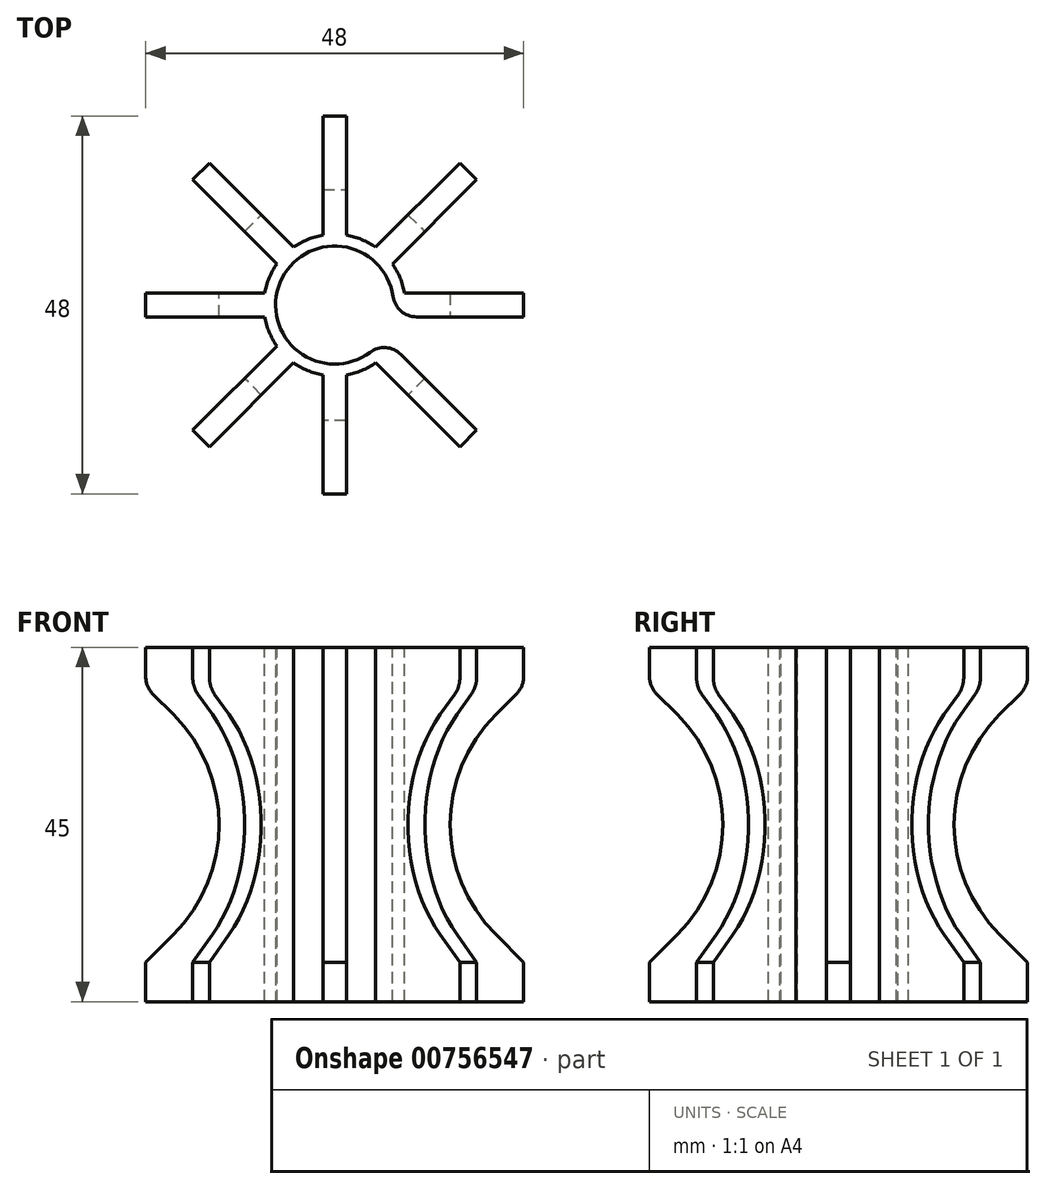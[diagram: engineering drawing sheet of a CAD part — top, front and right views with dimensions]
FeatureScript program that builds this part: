
annotation { "Feature Type Name" : "Feature", "Feature Type Description" : "" }
export const myFeature = defineFeature(function(context is Context, id is Id, definition is map)
    precondition{}
    {
        {
            assignVariable(context, id + "F0", {"name" : "h", "anyValue" : 45 * mm});
        }
        {
            assignVariable(context, id + "F1", {"name" : "t", "anyValue" : 1.5 * mm});
        }
        {
            assignVariable(context, id + "F2", {"name" : "fins", "anyValue" : 8});
        }
        {
            var Q0;
            Q0=qCreatedBy(makeId("Top.planeOp"),FACE);
            var sketch = newSketch(context, id + "F3", { "sketchPlane" : qUnion([Q0])});
            skCircle(sketch, "E0", {"center": v(0, 0) * mm, "radius": 7.5 * mm});
            skSolve(sketch);
        }
        {
            var Q0;
            Q0=makeQuery(id+"F3.imprint","IMPRINT",FACE,{"disambiguationData":[TD([[makeQuery(id+"F3.imprint","IMPRINT",EDGE,{"derivedFrom":sQuery(id+"F3.wireOp",EDGE,"E0")}),1.0]])]});
            extrude(context, id + "F4", {"entities" : qUnion([Q0]), "depth" : getVariable(context, 'h'), "offsetDistance" : 25 * mm});
        }
        {
            var Q0;
            Q0=makeQuery(id+"F4.opExtrude","CAP_FACE",FACE,{"disambiguationData":[OSD([sQuery(id+"F3.wireOp",EDGE,"E0")])],"isStart":false});
            var Q1;
            Q1=makeQuery(id+"F4.opExtrude","CAP_FACE",FACE,{"disambiguationData":[OSD([sQuery(id+"F3.wireOp",EDGE,"E0")])],"isStart":true});
            shell(context, id + "F5", {"entities" : qUnion([Q0, Q1]), "thickness" : getVariable(context, 't'), "oppositeDirection" : true});
        }
        {
            var Q0;
            Q0=makeQuery(id+"F4.opExtrude","CAP_FACE",FACE,{"disambiguationData":[OSD([sQuery(id+"F3.wireOp",EDGE,"E0")])],"isStart":false});
            var sketch = newSketch(context, id + "F6", { "sketchPlane" : qUnion([Q0])});
            skLineSegment(sketch, "E1.bottom", {"start": v(-1.5, 8.87) * mm, "end": v(1.5, 8.87) * mm});
            skLineSegment(sketch, "E1.top", {"start": v(-1.5, 24) * mm, "end": v(1.5, 24) * mm});
            skLineSegment(sketch, "E1.left", {"start": v(-1.5, 8.87) * mm, "end": v(-1.5, 24) * mm});
            skLineSegment(sketch, "E1.right", {"start": v(1.5, 8.87) * mm, "end": v(1.5, 24) * mm});
            skSolve(sketch);
        }
        {
            var Q0;
            Q0=qCreatedBy(makeId("Front.planeOp"),FACE);
            var sketch = newSketch(context, id + "F7", { "sketchPlane" : qUnion([Q0])});
            skLineSegment(sketch, "E2", {"start": v(0, 0) * mm, "end": v(0, 40.18) * mm});
            skSolve(sketch);
        }
        {
            var Q0;
            Q0 = qSketchRegion(id + "F6", true);
            var Q1;
            Q1=makeQuery(id+"F4.opExtrude","CAP_FACE",FACE,{"disambiguationData":[OSD([sQuery(id+"F3.wireOp",EDGE,"E0")])],"isStart":true});
            extrude(context, id + "F8", {"entities" : qUnion([Q0]), "operationType" : NewBodyOperationType.ADD, "endBound" : BoundingType.UP_TO_SURFACE, "oppositeDirection" : true, "depth" : 25 * mm, "endBoundEntityFace" : qUnion([Q1]), "offsetDistance" : 25 * mm});
        }
        {
            var Q0;
            Q0=makeQuery(id+"F8.opExtrude","SWEPT_FACE",FACE,{"disambiguationData":[OSD([sQuery(id+"F6.wireOp",EDGE,"E1.right")])]});
            var sketch = newSketch(context, id + "F9", { "sketchPlane" : qUnion([Q0])});
            skLineSegment(sketch, "E3", {"start": v(24, 5) * mm, "end": v(20.46, 8.54) * mm});
            skLineSegment(sketch, "E4", {"start": v(24, 40) * mm, "end": v(20.46, 36.46) * mm});
            skArc(sketch, "E5", {"start": v(20.46, 36.46) * mm, "mid": v(14.68, 22.5) * mm, "end": v(20.46, 8.54) * mm});
            skLineSegment(sketch, "E6", {"start": v(24, 5) * mm, "end": v(24, 40) * mm});
            skSolve(sketch);
        }
        {
            var Q0;
            Q0 = qSketchRegion(id + "F9", true);
            extrude(context, id + "F10", {"entities" : qUnion([Q0]), "operationType" : NewBodyOperationType.REMOVE, "endBound" : BoundingType.THROUGH_ALL, "oppositeDirection" : true, "depth" : 25 * mm, "offsetDistance" : 25 * mm});
        }
        {
            var Q0;
            Q0=makeQuery(id+"F10.boolean.opBoolean","COPY",EDGE,{"derivedFrom":makeQuery(id+"F10.opExtrude","SWEPT_EDGE",EDGE,{"disambiguationData":[OSD([sQuery(id+"F6.wireOp",EDGE,"E1.top"),sQuery(id+"F6.wireOp",EDGE,"E1.right"),sQuery(id+"F9.wireOp",EDGE,"E4"),sQuery(id+"F9.wireOp",EDGE,"E6")])]})});
            var Q1;
            Q1=makeQuery(id+"F10.boolean.opBoolean","COPY",EDGE,{"derivedFrom":makeQuery(id+"F10.opExtrude","SWEPT_EDGE",EDGE,{"disambiguationData":[OSD([sQuery(id+"F6.wireOp",EDGE,"E1.top"),sQuery(id+"F6.wireOp",EDGE,"E1.right"),sQuery(id+"F9.wireOp",EDGE,"E3"),sQuery(id+"F9.wireOp",EDGE,"E6")])]})});
            var Q2;
            Q2=makeQuery(id+"F8.opExtrude","SWEPT_EDGE",EDGE,{"disambiguationData":[OSD([sQuery(id+"F3.wireOp",EDGE,"E0"),sQuery(id+"F6.wireOp",EDGE,"E1.bottom"),sQuery(id+"F6.wireOp",EDGE,"E1.right")])]});
            var Q3;
            Q3=makeQuery(id+"F8.opExtrude","SWEPT_EDGE",EDGE,{"disambiguationData":[OSD([sQuery(id+"F3.wireOp",EDGE,"E0"),sQuery(id+"F6.wireOp",EDGE,"E1.bottom"),sQuery(id+"F6.wireOp",EDGE,"E1.left")])]});
            fillet(context, id + "F11", {"entities" : qUnion([Q0, Q1, Q2, Q3]), "radius" : getVariable(context, 't') * 2, "tangentPropagation" : true, "allowEdgeOverflow" : false});
        }
        {
            var Q0;
            Q0=makeQuery(id+"F4.opExtrude","SWEPT_BODY",BODY,{"disambiguationData":[OSD([sQuery(id+"F3.wireOp",EDGE,"E0")])]});
            var Q1;
            Q1=sQuery(id+"F7.wireOp",EDGE,"E2");
            circularPattern(context, id + "F12", {"operationType" : NewBodyOperationType.ADD, "entities" : qUnion([Q0]), "axis" : qUnion([Q1]), "angle" : 360 * degree, "instanceCount" : getVariable(context, 'fins'), "equalSpace" : true});
        }
        {
            var Q0;
            {var subQ0=makeQuery(id+"F8.opExtrude","CAP_FACE",FACE,{"disambiguationData":[OSD([sQuery(id+"F6.wireOp",EDGE,"E1.bottom"),sQuery(id+"F6.wireOp",EDGE,"E1.top"),sQuery(id+"F6.wireOp",EDGE,"E1.left"),sQuery(id+"F6.wireOp",EDGE,"E1.right")])],"isStart":true});Q0=makeQuery(id+"F12.boolean.opBoolean","MERGE",FACE,{"derivedFrom":[makeQuery(id+"F4.opExtrude","CAP_FACE",FACE,{"disambiguationData":[OSD([sQuery(id+"F3.wireOp",EDGE,"E0")])],"isStart":false}),subQ0,makeQuery(id+"F12.opPattern","COPY",FACE,{"derivedFrom":subQ0,"instanceName":"1"}),makeQuery(id+"F12.opPattern","COPY",FACE,{"derivedFrom":subQ0,"instanceName":"2"}),makeQuery(id+"F12.opPattern","COPY",FACE,{"derivedFrom":subQ0,"instanceName":"3"}),makeQuery(id+"F12.opPattern","COPY",FACE,{"derivedFrom":subQ0,"instanceName":"4"}),makeQuery(id+"F12.opPattern","COPY",FACE,{"derivedFrom":subQ0,"instanceName":"5"}),makeQuery(id+"F12.opPattern","COPY",FACE,{"derivedFrom":subQ0,"instanceName":"6"}),makeQuery(id+"F12.opPattern","COPY",FACE,{"derivedFrom":subQ0,"instanceName":"7"})]});}
            var sketch = newSketch(context, id + "F13", { "sketchPlane" : qUnion([Q0])});
            skLineSegment(sketch, "E7", {"start": v(18.03, -15.9) * mm, "end": v(3.62, -1.5) * mm});
            skLineSegment(sketch, "E8", {"start": v(24, -1.5) * mm, "end": v(3.62, -1.5) * mm});
            skLineSegment(sketch, "E9", {"start": v(18.03, -15.9) * mm, "end": v(24, -1.5) * mm});
            skSolve(sketch);
        }
        {
            var Q0;
            Q0 = qSketchRegion(id + "F13", true);
            extrude(context, id + "F14", {"entities" : qUnion([Q0]), "operationType" : NewBodyOperationType.REMOVE, "endBound" : BoundingType.THROUGH_ALL, "oppositeDirection" : true, "depth" : 25 * mm, "offsetDistance" : 25 * mm});
        }
        {
            var Q0;
            Q0=makeQuery(id+"F14.boolean.opBoolean","INTERSECT",EDGE,{"derivedFrom":[makeQuery(id+"F5.opShell","OFFSET_FACE",FACE,{"disambiguationData":[OSD([sQuery(id+"F3.wireOp",EDGE,"E0")])]}),makeQuery(id+"F14.opExtrude","SWEPT_FACE",FACE,{"disambiguationData":[OSD([sQuery(id+"F13.wireOp",EDGE,"E8")])]})]});
            var Q1;
            Q1=makeQuery(id+"F14.boolean.opBoolean","INTERSECT",EDGE,{"derivedFrom":[makeQuery(id+"F5.opShell","OFFSET_FACE",FACE,{"disambiguationData":[OSD([sQuery(id+"F3.wireOp",EDGE,"E0")])]}),makeQuery(id+"F14.opExtrude","SWEPT_FACE",FACE,{"disambiguationData":[OSD([sQuery(id+"F13.wireOp",EDGE,"E7")])]})]});
            fillet(context, id + "F15", {"entities" : qUnion([Q0, Q1]), "radius" : getVariable(context, 't') * 2, "tangentPropagation" : true, "allowEdgeOverflow" : false});
        }
    });
